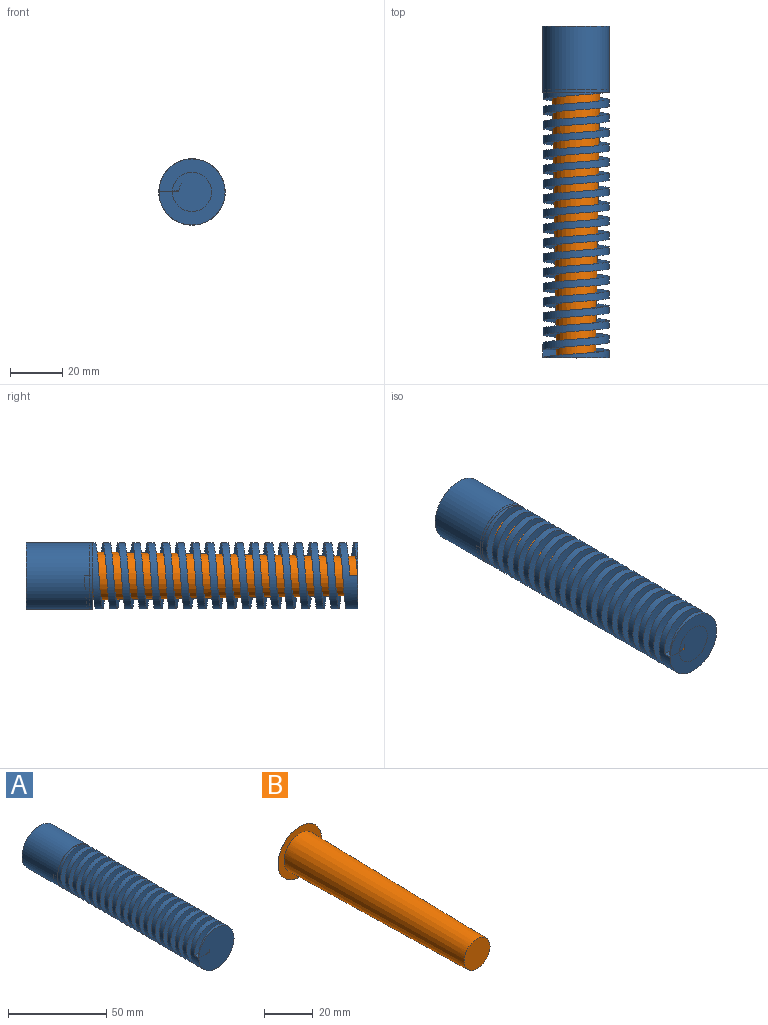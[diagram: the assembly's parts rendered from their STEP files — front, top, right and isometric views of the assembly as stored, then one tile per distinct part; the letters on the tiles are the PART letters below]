
ASSEMBLY  parts=2 mates=1
PART A: 28 faces, bbox 25.4x127.1x29.2 mm
  f0: cylinder r=12.64mm len=25.27mm, axis (0,1,0), area 330.3mm2, adj f1,f18,f23,f25,f27
  f1: cylinder r=12.64mm len=25.27mm, axis (0,1,0), area 211.4mm2, adj f0,f2,f25,f27
  f2: cylinder r=12.64mm len=25.27mm, axis (0,1,0), area 211.4mm2, adj f1,f3,f25,f27
  f3: cylinder r=12.64mm len=25.27mm, axis (0,1,0), area 211.4mm2, adj f2,f4,f25,f27
  f4: cylinder r=12.64mm len=25.27mm, axis (0,1,0), area 211.4mm2, adj f3,f5,f25,f27
  f5: cylinder r=12.64mm len=25.27mm, axis (0,1,0), area 211.4mm2, adj f4,f6,f25,f27
  f6: cylinder r=12.64mm len=25.27mm, axis (0,1,0), area 211.4mm2, adj f5,f7,f25,f27
  f7: cylinder r=12.64mm len=25.27mm, axis (0,1,0), area 211.3mm2, adj f6,f8,f25,f27
  f8: cylinder r=12.64mm len=25.27mm, axis (0,1,0), area 211.3mm2, adj f7,f9,f25,f27
  f9: cylinder r=12.64mm len=25.27mm, axis (0,1,0), area 211.3mm2, adj f8,f10,f25,f27
  f10: cylinder r=12.64mm len=25.27mm, axis (0,1,0), area 211.3mm2, adj f9,f11,f25,f27
  f11: cylinder r=12.64mm len=25.27mm, axis (0,1,0), area 211.4mm2, adj f10,f12,f25,f27
  f12: cylinder r=12.64mm len=25.27mm, axis (0,1,0), area 211.4mm2, adj f11,f13,f25,f27
  f13: cylinder r=12.64mm len=25.27mm, axis (0,1,0), area 211.3mm2, adj f12,f14,f25,f27
  f14: cylinder r=12.64mm len=25.27mm, axis (0,1,0), area 211.4mm2, adj f13,f15,f25,f27
  f15: cylinder r=12.64mm len=25.27mm, axis (0,1,0), area 211.4mm2, adj f14,f16,f25,f27
  f16: cylinder r=12.64mm len=25.27mm, axis (0,1,0), area 211.4mm2, adj f15,f17,f25,f27
  f17: cylinder r=12.64mm len=25.27mm, axis (0,1,0), area 161.6mm2, adj f16,f20,f25,f27
  f18: plane 25.3x25.3mm, normal (0,-1,0), area 500.4mm2, adj f0,f23,f24,f25
  f19: cylinder r=12.7mm len=25.4mm, axis (0,1,0), area 2026.8mm2, adj f20,f21
  f20: plane 25.4x25.4mm, normal (0,-1,0), area 5.1mm2, adj f17,f19,f26
  f21: plane 25.4x25.4mm, normal (0,1,0), area 506.7mm2, adj f19
  f22: plane 7.62x3.24mm, normal (0,0,-1), area 23.7mm2, adj f24,f25,f26,f27
  f23: plane 7.62x3.13mm, normal (0,0,1), area 23.5mm2, adj f0,f18,f24,f25,f27
  f24: cylinder r=5.02mm len=104.73mm, axis (0,-1,0), area 1889.9mm2, adj f18,f22,f23,f25,f27
  f25: bspline ~101.86x29.18mm, area 7652.4mm2, adj f0,f1,f2,f3,f4,f5,f6,f7
  f26: cylinder r=12.64mm len=25.27mm, axis (0,-1,0), area 69mm2, adj f20,f22,f25,f27
  f27: bspline ~101.6x29.18mm, area 7654.7mm2, adj f0,f1,f2,f3,f4,f5,f6,f7
PART B: 5 faces, bbox 25.4x102.8x25.4 mm
  f0: plane 15x15mm, normal (0,-1,0), area 176.7mm2, adj f4
  f1: plane 25.4x25.4mm, normal (0,1,0), area 506.7mm2, adj f2
  f2: cylinder r=12.7mm len=25.4mm, axis (0,-1,0), area 2mm2, adj f1,f3
  f3: plane 25.4x25.4mm, normal (0,-1,0), area 240.4mm2, adj f2,f4
  f4: cone r=7.5mm half-angle=1deg, axis (0,1,0), area 5392.8mm2, adj f0,f3
PLACE A at identity fixed
PLACE B t=(0,0.4,-39.25)mm
MATE fastened B.f2 <-> A.f0  axis (0,-1,0) through (0,-127,0)mm
